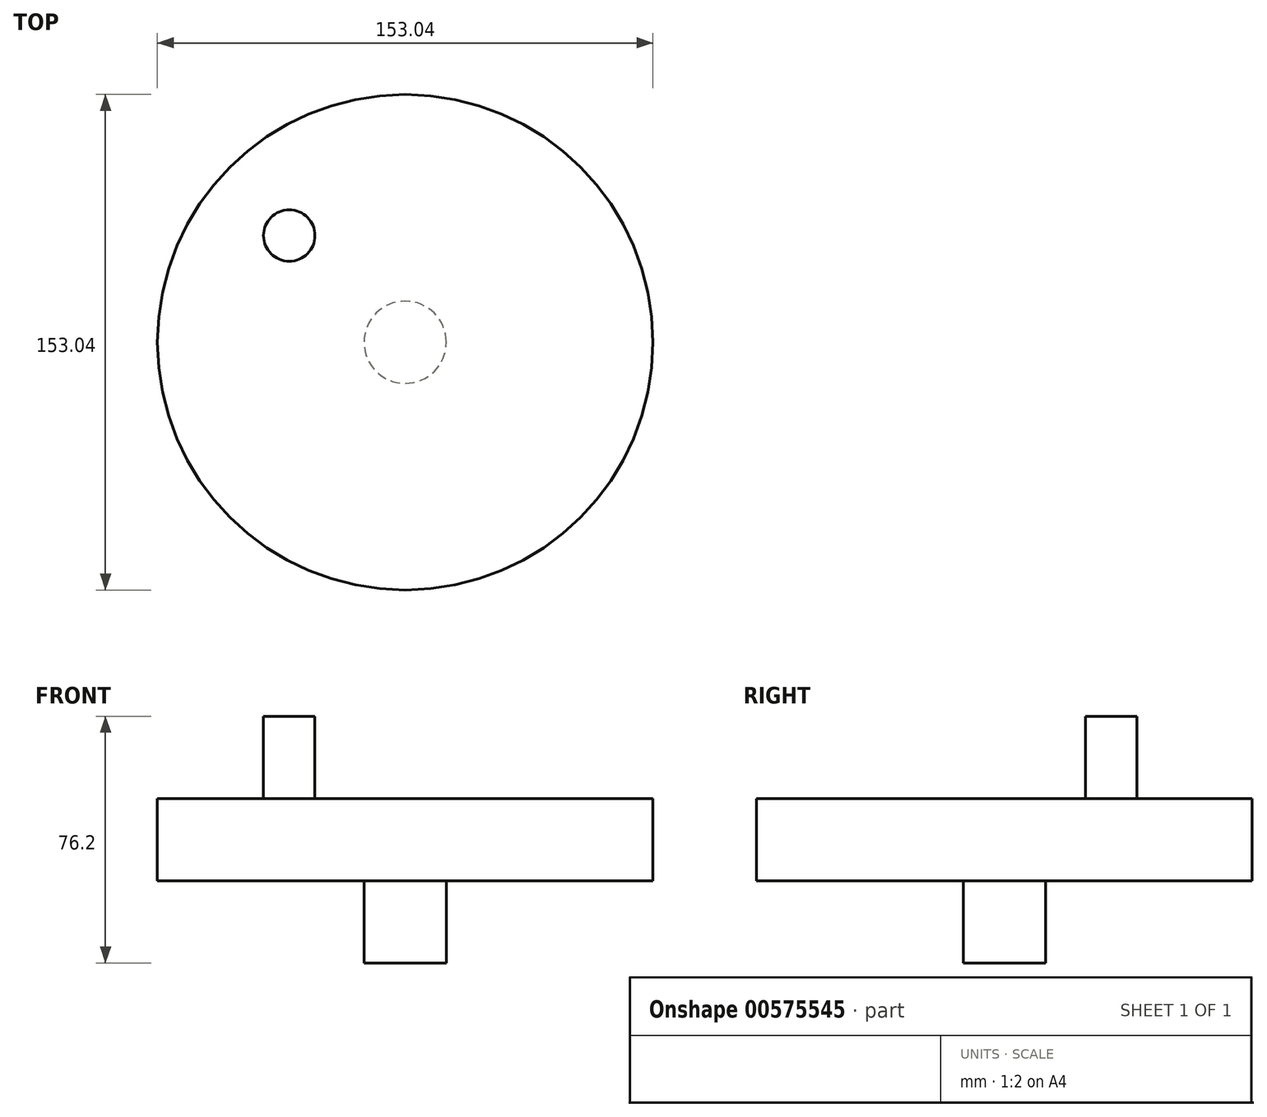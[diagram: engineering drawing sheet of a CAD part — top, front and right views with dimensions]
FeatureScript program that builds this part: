
annotation { "Feature Type Name" : "Feature", "Feature Type Description" : "" }
export const myFeature = defineFeature(function(context is Context, id is Id, definition is map)
    precondition{}
    {
        {
            var Q0;
            Q0=qCreatedBy(makeId("Top.planeOp"),FACE);
            var sketch = newSketch(context, id + "F0", { "sketchPlane" : qUnion([Q0])});
            skCircle(sketch, "E0", {"center": v(0, 0) * mm, "radius": 76.52 * mm});
            skSolve(sketch);
        }
        {
            var Q0;
            Q0=makeQuery(id+"F0.imprint","IMPRINT",FACE,{"disambiguationData":[TD([[makeQuery(id+"F0.imprint","IMPRINT",EDGE,{"derivedFrom":sQuery(id+"F0.wireOp",EDGE,"E0")}),1.0]])]});
            extrude(context, id + "F1", {"entities" : qUnion([Q0]), "depth" : 25.4 * mm, "offsetDistance" : 25.4 * mm});
        }
        {
            var Q0;
            Q0=qCreatedBy(makeId("Top.planeOp"),FACE);
            var sketch = newSketch(context, id + "F2", { "sketchPlane" : qUnion([Q0])});
            skCircle(sketch, "E1", {"center": v(-35.81, 32.96) * mm, "radius": 7.94 * mm});
            skSolve(sketch);
        }
        {
            var Q0;
            Q0 = qSketchRegion(id + "F2", true);
            extrude(context, id + "F3", {"entities" : qUnion([Q0]), "operationType" : NewBodyOperationType.ADD, "oppositeDirection" : true, "depth" : -50.8 * mm, "offsetDistance" : 25.4 * mm});
        }
        {
            var Q0;
            Q0=qCreatedBy(makeId("Top.planeOp"),FACE);
            var sketch = newSketch(context, id + "F4", { "sketchPlane" : qUnion([Q0])});
            skCircle(sketch, "E2", {"center": v(0, 0) * mm, "radius": 12.7 * mm});
            skSolve(sketch);
        }
        {
            var Q0;
            Q0 = qSketchRegion(id + "F4", true);
            extrude(context, id + "F5", {"entities" : qUnion([Q0]), "operationType" : NewBodyOperationType.ADD, "oppositeDirection" : true, "depth" : 25.4 * mm, "offsetDistance" : 25.4 * mm});
        }
    });
